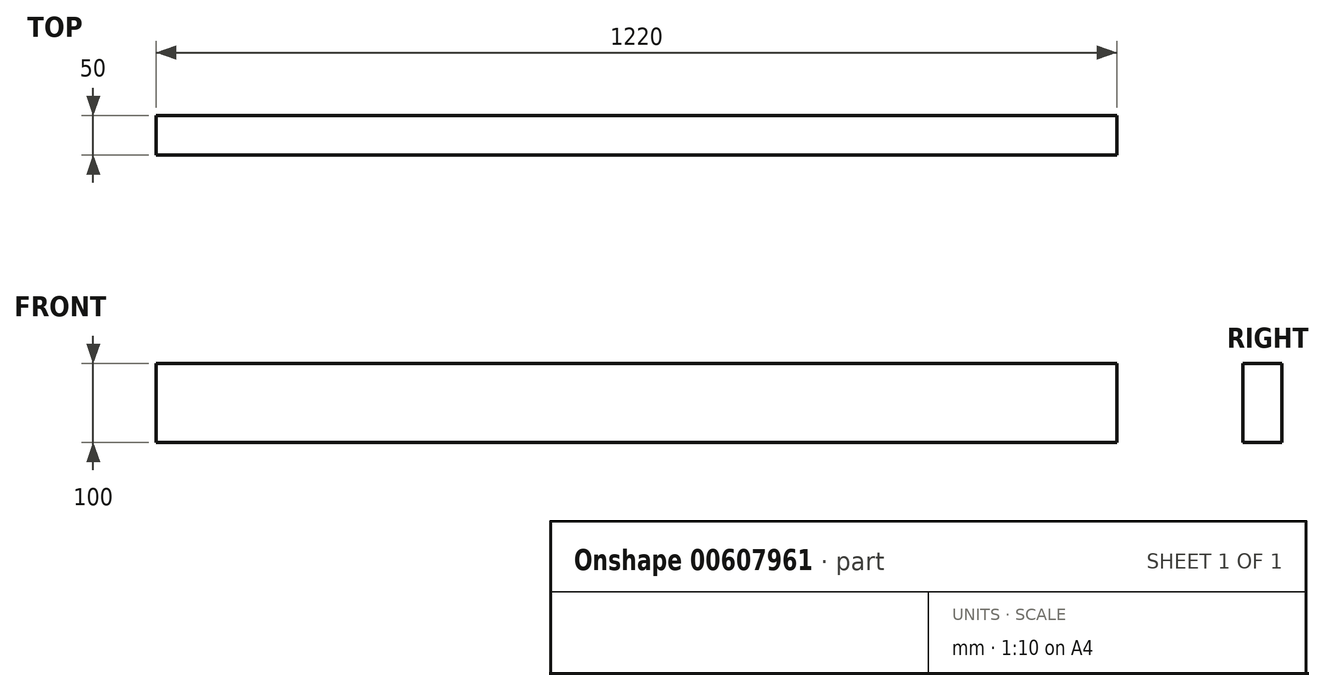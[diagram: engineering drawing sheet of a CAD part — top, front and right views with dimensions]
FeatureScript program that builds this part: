
annotation { "Feature Type Name" : "Feature", "Feature Type Description" : "" }
export const myFeature = defineFeature(function(context is Context, id is Id, definition is map)
    precondition{}
    {
        {
            var Q0;
            Q0=qCreatedBy(makeId("Front.planeOp"),FACE);
            var sketch = newSketch(context, id + "F0", { "sketchPlane" : qUnion([Q0])});
            skLineSegment(sketch, "E0.bottom", {"start": v(-610.08, 46.26) * mm, "end": v(609.92, 46.26) * mm});
            skLineSegment(sketch, "E0.top", {"start": v(-610.08, -53.74) * mm, "end": v(609.92, -53.74) * mm});
            skLineSegment(sketch, "E0.left", {"start": v(-610.08, 46.26) * mm, "end": v(-610.08, -53.74) * mm});
            skLineSegment(sketch, "E0.right", {"start": v(609.92, 46.26) * mm, "end": v(609.92, -53.74) * mm});
            skSolve(sketch);
        }
        {
            var Q0;
            Q0 = qSketchRegion(id + "F0", true);
            extrude(context, id + "F1", {"entities" : qUnion([Q0]), "depth" : 50 * mm, "offsetDistance" : 25 * mm});
        }
    });
